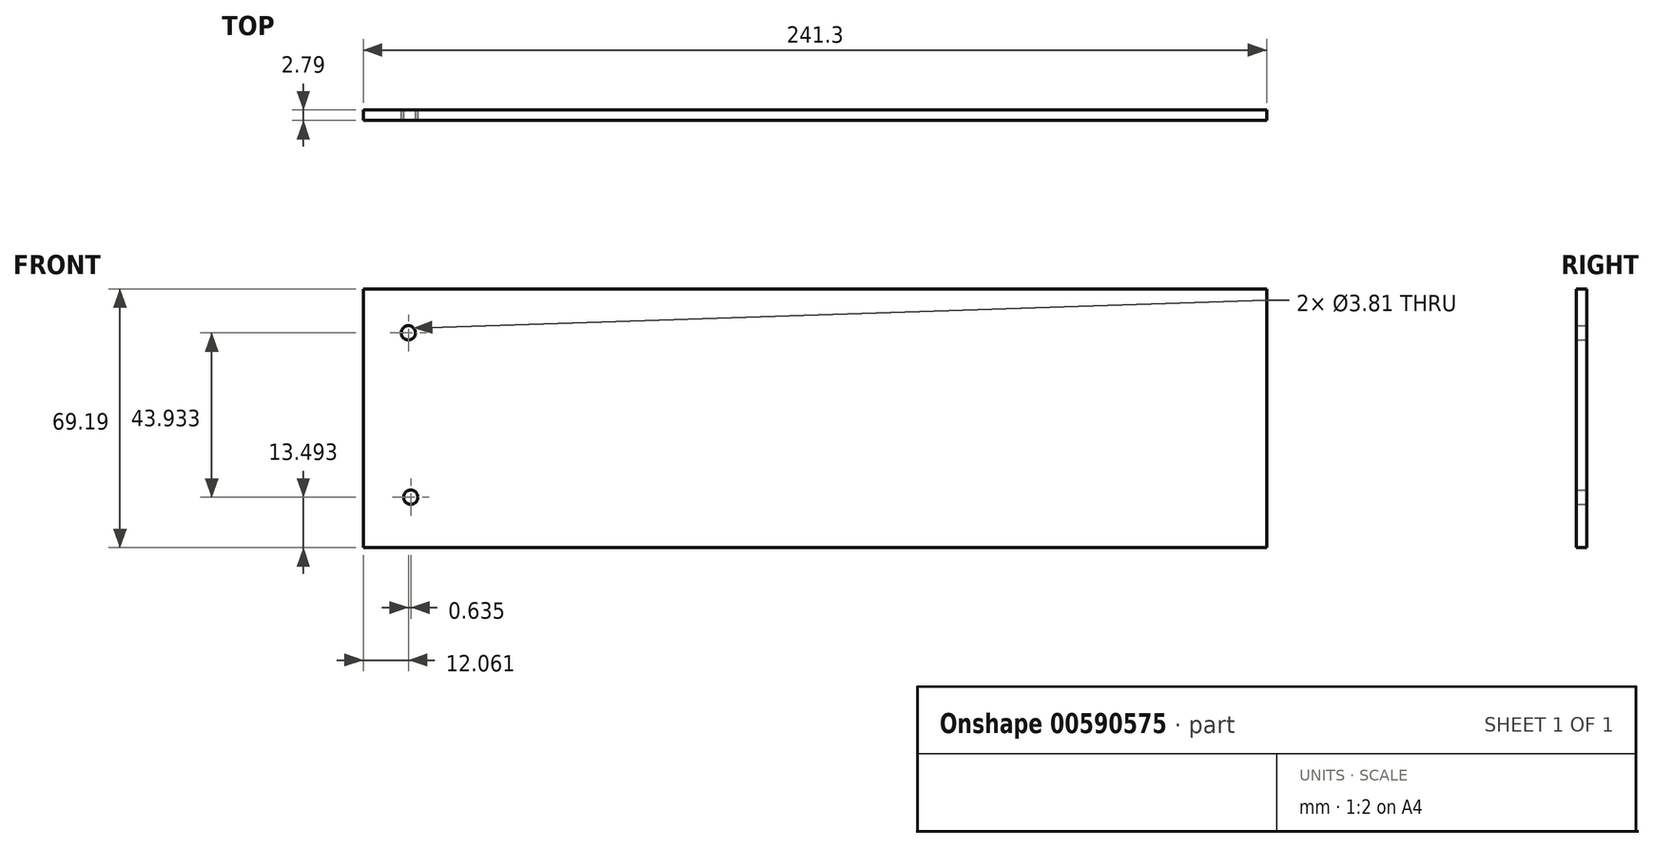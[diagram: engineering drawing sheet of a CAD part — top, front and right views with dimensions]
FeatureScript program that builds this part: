
annotation { "Feature Type Name" : "Feature", "Feature Type Description" : "" }
export const myFeature = defineFeature(function(context is Context, id is Id, definition is map)
    precondition{}
    {
        {
            var Q0;
            Q0=qCreatedBy(makeId("Front.planeOp"),FACE);
            var sketch = newSketch(context, id + "F0", { "sketchPlane" : qUnion([Q0])});
            skLineSegment(sketch, "E0.bottom", {"start": v(-65.3, 46.54) * mm, "end": v(176, 46.54) * mm});
            skLineSegment(sketch, "E0.top", {"start": v(-65.3, -22.65) * mm, "end": v(176, -22.65) * mm});
            skLineSegment(sketch, "E0.left", {"start": v(-65.3, 46.54) * mm, "end": v(-65.3, -22.65) * mm});
            skLineSegment(sketch, "E0.right", {"start": v(176, 46.54) * mm, "end": v(176, -22.65) * mm});
            skCircle(sketch, "E1", {"center": v(-53.24, 34.78) * mm, "radius": 1.9 * mm});
            skCircle(sketch, "E2", {"center": v(-52.6, -9.16) * mm, "radius": 1.9 * mm});
            skSolve(sketch);
        }
        {
            var Q0;
            Q0=makeQuery(id+"F0.imprint","IMPRINT",FACE,{"disambiguationData":[TD([[makeQuery(id+"F0.imprint","IMPRINT",EDGE,{"derivedFrom":sQuery(id+"F0.wireOp",EDGE,"E0.bottom")}),-1.0]])]});
            extrude(context, id + "F1", {"entities" : qUnion([Q0]), "depth" : 2.8 * mm, "offsetDistance" : 25.4 * mm});
        }
    });
